# Revit family: NLRS_57_DUA_UN_Jaloezieklep_LT_KxVTFx_Solid_Air
name_source: partatom
category: Duct Accessories
units: mm (PartAtom-declared; Revit-internal decimal feet)

## family parameters
Always vertical = Yes
Cut with Voids When Loaded = No
OmniClass Number = 23.75.70.14.34
OmniClass Title = Air Duct Accessories
Part Type = Breaks Into
Round Connector Dimension = Use Diameter
Shared = No
Work Plane-Based = No

## types (6) — shared parameters
Assembly Code = 57.00
Manufacturer = Solid Air Climate Solutions
NLRS_C_content_datum_uitgifte = 23-05-2023
NLRS_C_content_provider = Solid Air Climate Solutions
NLRS_C_content_versie = 3.20.00
SACS_Data_Hidden = K_VTFx
URL = https://solid-air.nl
zero-valued in all types: Default Elevation

## per-type parameters (varying)
| type | Description | SACS_Index1 | SACS_Index2 | SACS_Option_1 | SACS_Option_2 | Type Comments |
| KIVTFH | Volume damper suitable for manual operation | 0 mm  [stored 0 ft] | 0 mm  [stored 0 ft] | Standard (I) | Manual operation (H) | Maximum size: 2000x1995 |
| KIVTFG | Volume damper suitable for motorized operation | 0 mm  [stored 0 ft] | 1 mm  [stored 0.00328084 ft] | Standard (I) | Suitable for motorized operation (G) | Maximum size: 2000x1995 |
| KRVTFH | Volume damper suitable for manual operation | 1 mm  [stored 0.00328084 ft] | 0 mm  [stored 0 ft] | Rubber seal on air-blades (R) | Manual operation (H) | Maximum size: 1600x1995 |
| KRVTFG | Volume damper suitable for motorized operation | 1 mm  [stored 0.00328084 ft] | 1 mm  [stored 0.00328084 ft] | Rubber seal on air-blades (R) | Suitable for motorized operation (G) | Maximum size: 1600x1995 |
| KLVTFH | Volume damper suitable for manual operation | 2 mm  [stored 0.00656168 ft] | 0 mm  [stored 0 ft] | Air-tight class 4 according EN 1751 (L) | Manual operation (H) | Maximum size: 1600x1995 |
| KLVTFG | Volume damper suitable for motorized operation | 2 mm  [stored 0.00656168 ft] | 1 mm  [stored 0.00328084 ft] | Air-tight class 4 according EN 1751 (L) | Suitable for motorized operation (G) | Maximum size: 1600x1995 |

note: column(s) folded — value = type name in every type: Model

note: [stored X ft] marks values corroborated as IEEE doubles in the binary element streams (Revit-internal decimal feet)

## geometry (parser evidence)
native form markers: Sweep x9
no freeform markers — native parametric forms only
